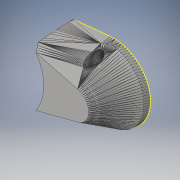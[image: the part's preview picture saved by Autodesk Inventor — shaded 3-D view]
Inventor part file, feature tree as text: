
AUTODESK INVENTOR PART (.ipt)
format: ipt  version: 2019.2 (Build 232265000, 265)  size: 2,024,448 bytes
history: native  units: mm
features: other x2, sketch x1
ambient origin geometry x8: Origin, YZ Plane, XZ Plane, XY Plane, X Axis, Y Axis, Z Axis, Center Point
bodies: Solid1 (feature_tree)
feature tree (3):
  other  "V4PulleyCover"
  other  "MeshFeature1"
  sketch  "Sketch1"
